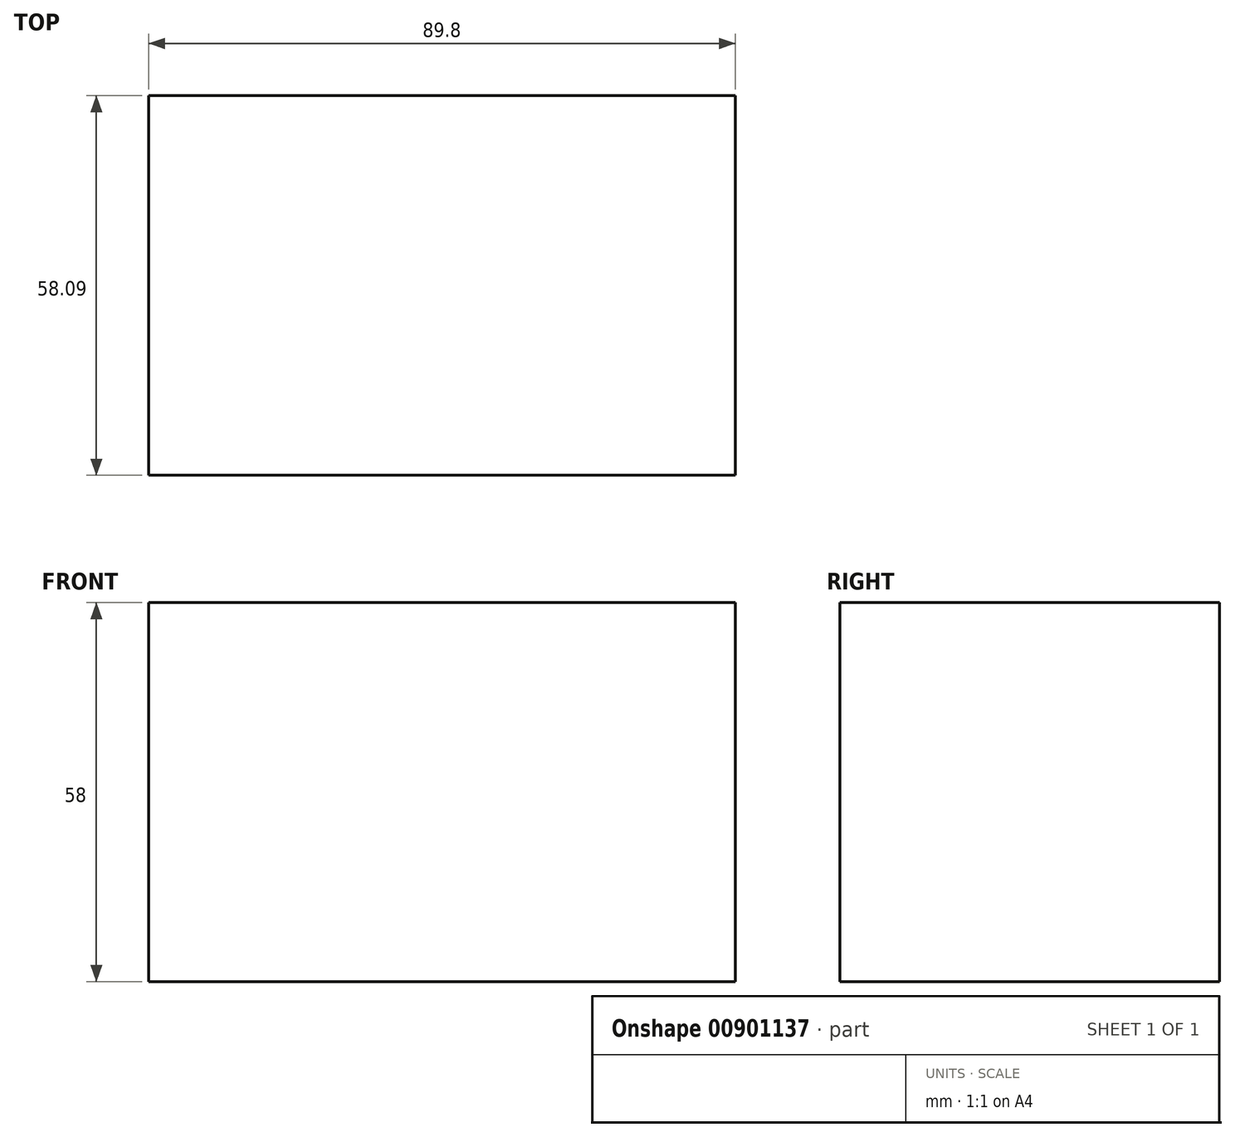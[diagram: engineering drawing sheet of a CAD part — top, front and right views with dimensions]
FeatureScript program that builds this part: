
annotation { "Feature Type Name" : "Feature", "Feature Type Description" : "" }
export const myFeature = defineFeature(function(context is Context, id is Id, definition is map)
    precondition{}
    {
        {
            var Q0;
            Q0=qCreatedBy(makeId("Top.planeOp"),FACE);
            var sketch = newSketch(context, id + "F0", { "sketchPlane" : qUnion([Q0])});
            skLineSegment(sketch, "E0.bottom", {"start": v(56.23, -21.03) * mm, "end": v(-33.57, -21.03) * mm});
            skLineSegment(sketch, "E0.top", {"start": v(56.23, 37.06) * mm, "end": v(-33.57, 37.06) * mm});
            skLineSegment(sketch, "E0.left", {"start": v(56.23, -21.03) * mm, "end": v(56.23, 37.06) * mm});
            skLineSegment(sketch, "E0.right", {"start": v(-33.57, -21.03) * mm, "end": v(-33.57, 37.06) * mm});
            skSolve(sketch);
        }
        {
            var Q0;
            Q0 = qSketchRegion(id + "F0", true);
            extrude(context, id + "F1", {"entities" : qUnion([Q0]), "depth" : 58 * mm, "offsetDistance" : 25 * mm});
        }
    });
